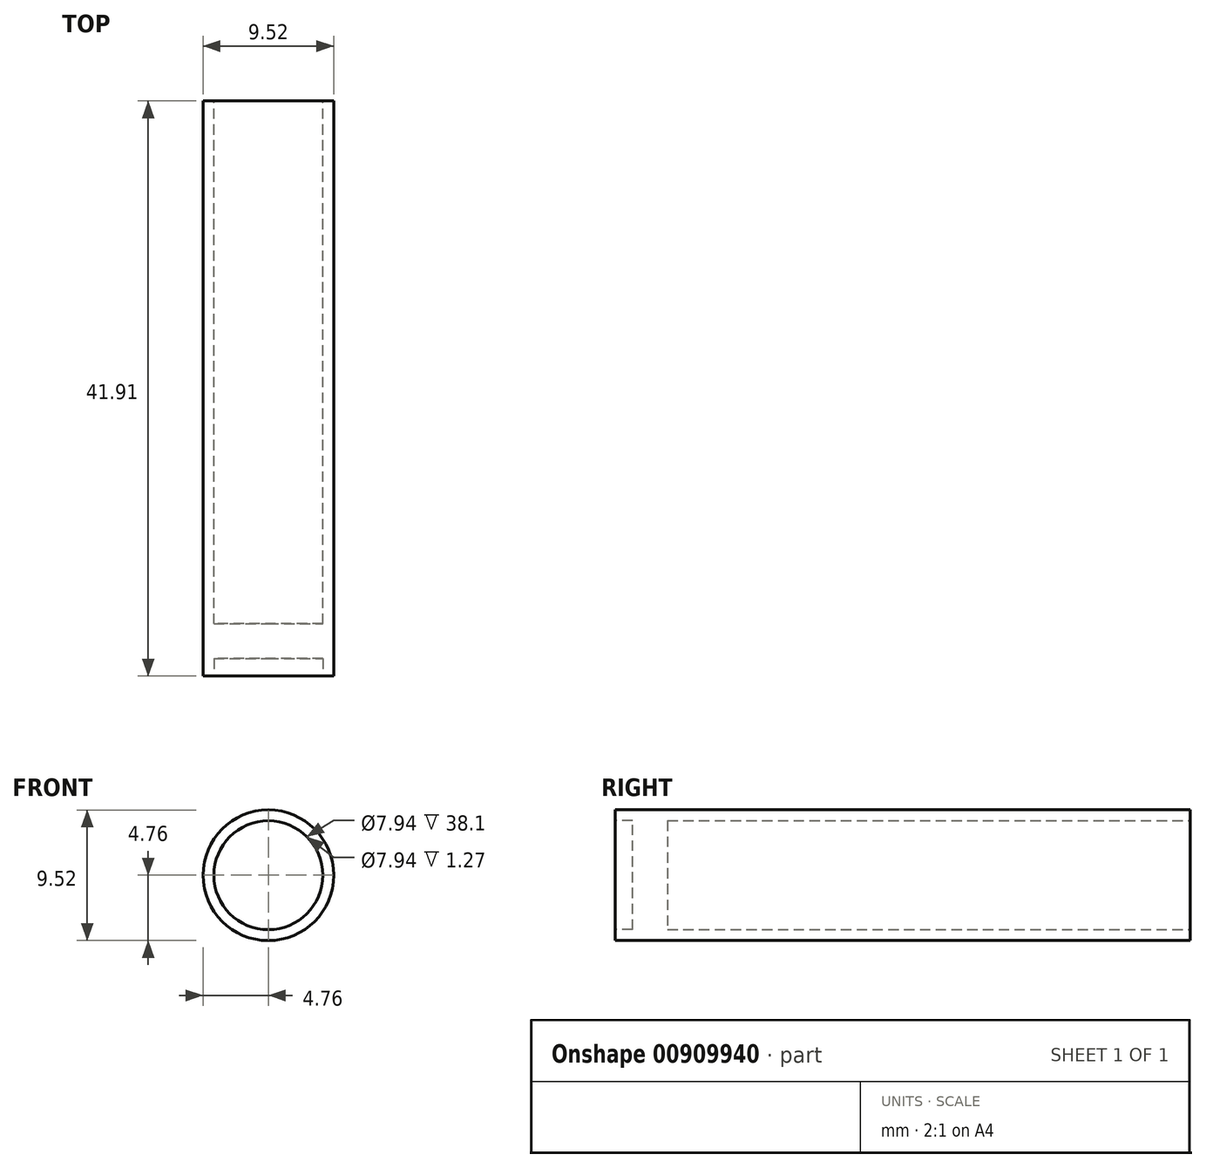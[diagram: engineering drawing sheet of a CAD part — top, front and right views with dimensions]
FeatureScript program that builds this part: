
annotation { "Feature Type Name" : "Feature", "Feature Type Description" : "" }
export const myFeature = defineFeature(function(context is Context, id is Id, definition is map)
    precondition{}
    {
        {
            var Q0;
            Q0=qCreatedBy(makeId("Front.planeOp"),FACE);
            var sketch = newSketch(context, id + "F0", { "sketchPlane" : qUnion([Q0])});
            skCircle(sketch, "E0", {"center": v(0, 0) * mm, "radius": 4.76 * mm});
            skSolve(sketch);
        }
        {
            var Q0;
            Q0=makeQuery(id+"F0.imprint","IMPRINT",FACE,{"disambiguationData":[TD([[makeQuery(id+"F0.imprint","IMPRINT",EDGE,{"derivedFrom":sQuery(id+"F0.wireOp",EDGE,"E0")}),1.0]])]});
            extrude(context, id + "F1", {"entities" : qUnion([Q0]), "depth" : 41.9 * mm, "offsetDistance" : 25.4 * mm});
        }
        {
            var Q0;
            Q0=makeQuery(id+"F1.opExtrude","CAP_FACE",FACE,{"disambiguationData":[OSD([sQuery(id+"F0.wireOp",EDGE,"E0")])],"isStart":true});
            var sketch = newSketch(context, id + "F2", { "sketchPlane" : qUnion([Q0])});
            skCircle(sketch, "E1", {"center": v(0, 0) * mm, "radius": 3.97 * mm});
            skSolve(sketch);
        }
        {
            var Q0;
            Q0 = qSketchRegion(id + "F2", true);
            extrude(context, id + "F3", {"entities" : qUnion([Q0]), "operationType" : NewBodyOperationType.REMOVE, "oppositeDirection" : true, "depth" : 38.1 * mm, "offsetDistance" : 25.4 * mm});
        }
        {
            var Q0;
            Q0=makeQuery(id+"F1.opExtrude","CAP_FACE",FACE,{"disambiguationData":[OSD([sQuery(id+"F0.wireOp",EDGE,"E0")])],"isStart":false});
            var sketch = newSketch(context, id + "F4", { "sketchPlane" : qUnion([Q0])});
            skCircle(sketch, "E2", {"center": v(0, 0) * mm, "radius": 3.97 * mm});
            skSolve(sketch);
        }
        {
            var Q0;
            Q0 = qSketchRegion(id + "F4", true);
            extrude(context, id + "F5", {"entities" : qUnion([Q0]), "operationType" : NewBodyOperationType.REMOVE, "oppositeDirection" : true, "depth" : 1.27 * mm, "offsetDistance" : 25.4 * mm});
        }
    });
